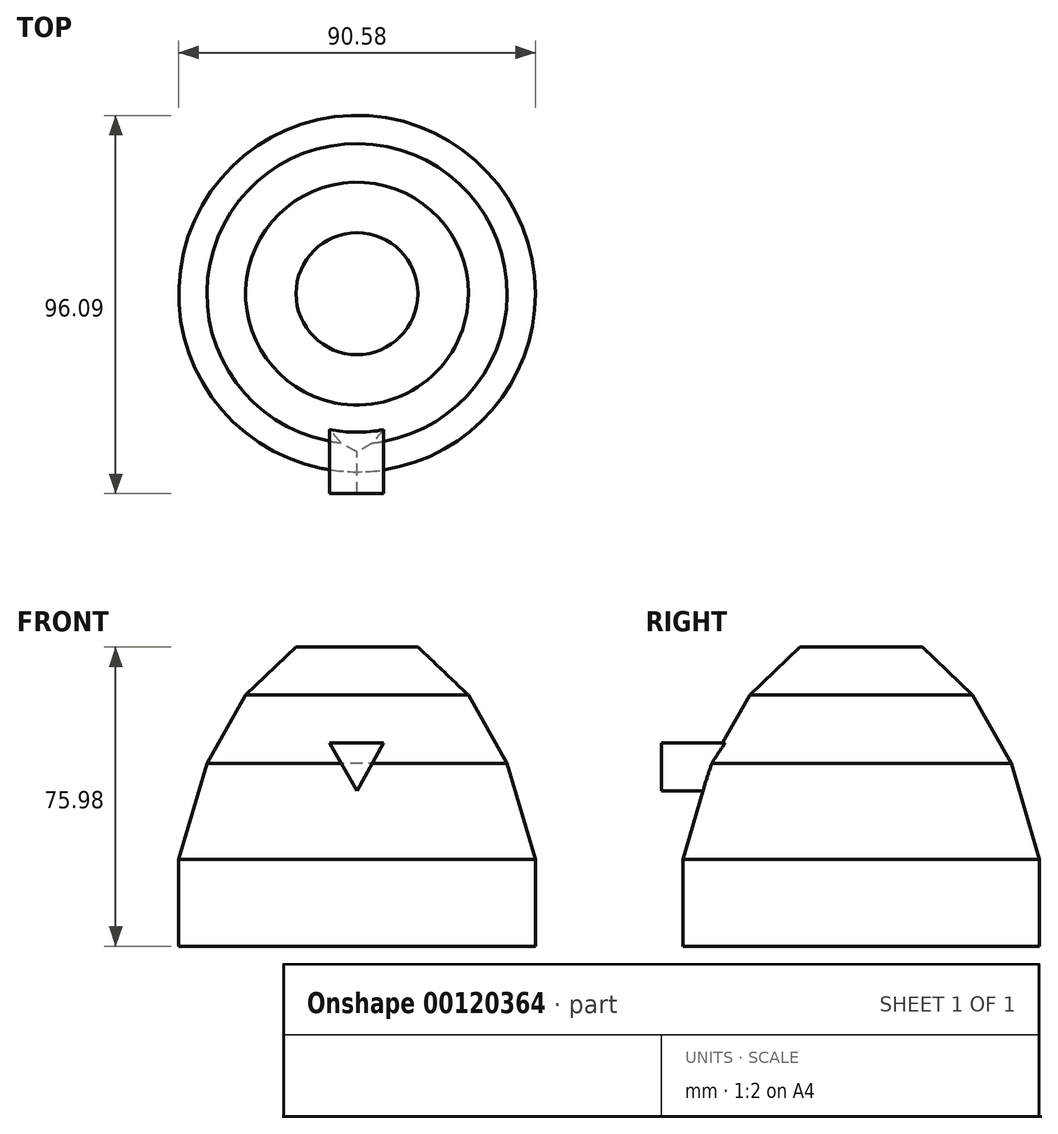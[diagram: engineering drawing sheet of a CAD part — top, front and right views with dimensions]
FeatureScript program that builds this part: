
annotation { "Feature Type Name" : "Feature", "Feature Type Description" : "" }
export const myFeature = defineFeature(function(context is Context, id is Id, definition is map)
    precondition{}
    {
        {
            var Q0;
            Q0=qCreatedBy(makeId("Front.planeOp"),FACE);
            var sketch = newSketch(context, id + "F0", { "sketchPlane" : qUnion([Q0])});
            skLineSegment(sketch, "E0", {"start": v(0, -32.03) * mm, "end": v(-45.3, -32.03) * mm});
            skLineSegment(sketch, "E1", {"start": v(-45.3, -32.03) * mm, "end": v(-45.3, -9.98) * mm});
            skLineSegment(sketch, "E2", {"start": v(-45.3, -9.98) * mm, "end": v(-38.14, 14.45) * mm});
            skLineSegment(sketch, "E3", {"start": v(-38.14, 14.45) * mm, "end": v(-28.3, 31.74) * mm});
            skLineSegment(sketch, "E4", {"start": v(-28.3, 31.74) * mm, "end": v(-15.5, 43.95) * mm});
            skLineSegment(sketch, "E5", {"start": v(-15.5, 43.95) * mm, "end": v(0, 43.95) * mm});
            skLineSegment(sketch, "E6", {"start": v(0, 43.95) * mm, "end": v(0, -32.03) * mm});
            skSolve(sketch);
        }
        {
            var Q0;
            Q0=makeQuery(id+"F0.imprint","IMPRINT",FACE,{"disambiguationData":[TD([[makeQuery(id+"F0.imprint","IMPRINT",EDGE,{"derivedFrom":sQuery(id+"F0.wireOp",EDGE,"E0")}),-1.0]])]});
            var Q1;
            Q1=sQuery(id+"F0.wireOp",EDGE,"E6");
            revolve(context, id + "F1", {"entities" : qUnion([Q0]), "axis" : qUnion([Q1]), "revolveType" : RevolveType.FULL});
        }
        {
            var Q0;
            Q0=qCreatedBy(makeId("Front.planeOp"),FACE);
            var sketch = newSketch(context, id + "F2", { "sketchPlane" : qUnion([Q0])});
            skLineSegment(sketch, "E7", {"start": v(-7.02, 19.6) * mm, "end": v(6.77, 19.6) * mm});
            skLineSegment(sketch, "E8", {"start": v(6.77, 19.6) * mm, "end": v(0, 7.46) * mm});
            skLineSegment(sketch, "E9", {"start": v(0, 7.46) * mm, "end": v(-7.02, 19.6) * mm});
            skSolve(sketch);
        }
        {
            var Q0;
            Q0 = qSketchRegion(id + "F2", true);
            extrude(context, id + "F3", {"entities" : qUnion([Q0]), "operationType" : NewBodyOperationType.ADD, "depth" : 50.8 * mm});
        }
    });
